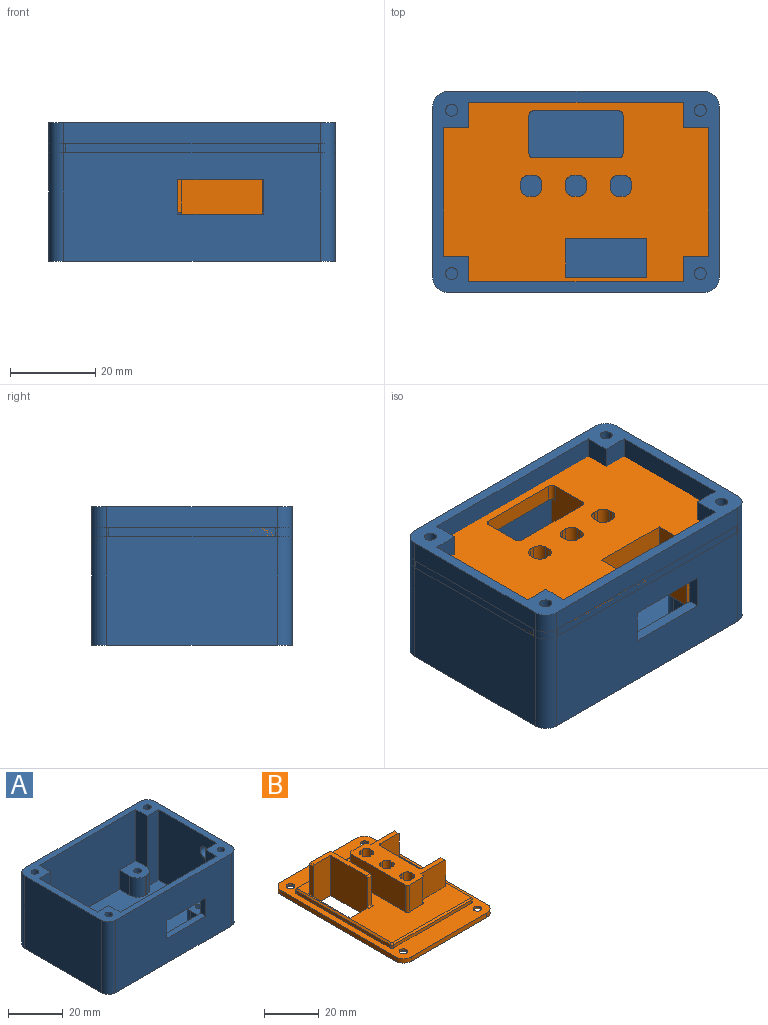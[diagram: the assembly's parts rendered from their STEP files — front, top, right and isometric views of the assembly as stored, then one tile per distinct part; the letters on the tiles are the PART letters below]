
ASSEMBLY  parts=2 mates=1
PART A: 64 faces, bbox 67x47x32.5 mm
  f0: plane 50.15x31.6mm, normal (0,1,0), area 1279mm2, adj f9,f13,f21,f23,f35,f36,f47,f50
  f1: plane 60x32.5mm, normal (0,-1,0), area 1790mm2, adj f13,f14,f17,f18,f59,f60,f61,f62
  f2: plane 50.15x31.6mm, normal (0,-1,0), area 1439mm2, adj f9,f13,f28,f32,f37,f38,f53,f56
  f3: plane 31.6x30.15mm, normal (1,0,0), area 952.7mm2, adj f9,f13,f26,f34
  f4: plane 31.6x30.15mm, normal (-1,0,0), area 933.1mm2, adj f9,f13,f19,f27,f63
  f5: plane 0.53x0.03mm, normal (0,0,1), area 0mm2, adj f27,f41,f53
  f6: plane 0.53x0.03mm, normal (0,0,1), area 0mm2, adj f26,f44,f50
  f7: plane 0.53x0.03mm, normal (0,0,1), area 0mm2, adj f34,f45,f56
  f8: plane 0.53x0.03mm, normal (0,0,1), area 0mm2, adj f19,f39,f47
  f9: plane 62x42mm, normal (0,0,1), area 2172.4mm2, adj f0,f2,f3,f4,f19,f20,f21,f23
  f10: plane 40x32.5mm, normal (1,0,0), area 1280.4mm2, adj f13,f14,f16,f17,f63
  f11: plane 60x32.5mm, normal (0,1,0), area 1950mm2, adj f13,f14,f15,f16
  f12: plane 40x32.5mm, normal (-1,0,0), area 1300mm2, adj f13,f14,f15,f18
  f13: plane 67x47mm, normal (0,0,1), area 650.3mm2, adj f0,f1,f2,f3,f4,f10,f11,f12
  f14: plane 67x47mm, normal (0,0,-1), area 3113.9mm2, adj f1,f10,f11,f12,f15,f16,f17,f18
  f15: cylinder r=3.5mm len=32.5mm, axis (0,0,1), area 178.7mm2, adj f11,f12,f13,f14
  f16: cylinder r=3.5mm len=32.5mm, axis (0,0,-1), area 178.7mm2, adj f10,f11,f13,f14
  f17: cylinder r=3.5mm len=32.5mm, axis (0,0,1), area 178.7mm2, adj f1,f10,f13,f14
  f18: cylinder r=3.5mm len=32.5mm, axis (0,0,-1), area 178.7mm2, adj f1,f12,f13,f14
  f19: plane 31.6x5.96mm, normal (0,1,0), area 187.3mm2, adj f4,f8,f9,f13,f39,f47
  f20: plane 8.6x0.48mm, normal (0,1,0), area 4.1mm2, adj f9,f35,f39,f40
  f21: plane 8.6x5.4mm, normal (-1,0,0), area 46.4mm2, adj f0,f9,f35,f40
  f22: cylinder r=1.4mm len=9.5mm, axis (0,0,1), area 83.6mm2, adj f14,f35
  f23: plane 8.6x5.4mm, normal (1,0,0), area 46.4mm2, adj f0,f9,f36,f43
  f24: plane 8.6x0.48mm, normal (0,1,0), area 4.1mm2, adj f9,f36,f43,f44
  f25: cylinder r=1.4mm len=9.5mm, axis (0,0,1), area 83.6mm2, adj f14,f36
  f26: plane 31.6x5.96mm, normal (0,1,0), area 187.3mm2, adj f3,f6,f9,f13,f44,f50
  f27: plane 31.6x5.96mm, normal (0,-1,0), area 187.3mm2, adj f4,f5,f9,f13,f41,f53
  f28: plane 8.6x5.4mm, normal (-1,0,0), area 46.4mm2, adj f2,f9,f37,f42
  f29: cylinder r=1.4mm len=9.5mm, axis (0,0,1), area 83.6mm2, adj f14,f37
  f30: plane 8.6x0.48mm, normal (0,-1,0), area 4.1mm2, adj f9,f37,f41,f42
  f31: plane 8.6x0.48mm, normal (0,-1,0), area 4.1mm2, adj f9,f38,f45,f46
  f32: plane 8.6x5.4mm, normal (1,0,0), area 46.4mm2, adj f2,f9,f38,f46
  f33: cylinder r=1.4mm len=9.5mm, axis (0,0,1), area 83.6mm2, adj f14,f38
  f34: plane 31.6x5.96mm, normal (0,-1,0), area 187.3mm2, adj f3,f7,f9,f13,f45,f56
  f35: plane 9.4x8.48mm, normal (0,0,1), area 66.6mm2, adj f0,f20,f21,f22,f39,f40,f47
  f36: plane 9.4x8.48mm, normal (0,0,1), area 66.6mm2, adj f0,f23,f24,f25,f43,f44,f50
  f37: plane 9.4x8.48mm, normal (0,0,1), area 66.6mm2, adj f2,f28,f29,f30,f41,f42,f53
  f38: plane 9.4x8.48mm, normal (0,0,1), area 66.6mm2, adj f2,f31,f32,f33,f45,f46,f56
  f39: cylinder r=4mm len=8.6mm, axis (0,0,-1), area 53.2mm2, adj f8,f9,f19,f20,f35,f47
  f40: cylinder r=4mm len=8.6mm, axis (0,0,1), area 54mm2, adj f9,f20,f21,f35
  f41: cylinder r=4mm len=8.6mm, axis (0,0,-1), area 53.2mm2, adj f5,f9,f27,f30,f37,f53
  f42: cylinder r=4mm len=8.6mm, axis (0,0,1), area 54mm2, adj f9,f28,f30,f37
  f43: cylinder r=4mm len=8.6mm, axis (0,0,1), area 54mm2, adj f9,f23,f24,f36
  f44: cylinder r=4mm len=8.6mm, axis (0,0,-1), area 53.2mm2, adj f6,f9,f24,f26,f36,f50
  f45: cylinder r=4mm len=8.6mm, axis (0,0,-1), area 53.2mm2, adj f7,f9,f31,f34,f38,f56
  f46: cylinder r=4mm len=8.6mm, axis (0,0,1), area 54mm2, adj f9,f31,f32,f38
  f47: plane 30x5.93mm, normal (-1,0,0), area 140mm2, adj f0,f8,f13,f19,f35,f39
  f48: plane 2.8x2.8mm, normal (0,0,1), area 6.2mm2, adj f49
  f49: cylinder r=1.4mm len=31.6mm, axis (0,0,1), area 278mm2, adj f13,f48
  f50: plane 30x5.93mm, normal (1,0,0), area 140mm2, adj f0,f6,f13,f26,f36,f44
  f51: plane 2.8x2.8mm, normal (0,0,1), area 6.2mm2, adj f52
  f52: cylinder r=1.4mm len=31.6mm, axis (0,0,1), area 278mm2, adj f13,f51
  f53: plane 30x5.93mm, normal (-1,0,0), area 140mm2, adj f2,f5,f13,f27,f37,f41
  f54: plane 2.8x2.8mm, normal (0,0,1), area 6.2mm2, adj f55
  f55: cylinder r=1.4mm len=31.6mm, axis (0,0,1), area 278mm2, adj f13,f54
  f56: plane 30x5.93mm, normal (1,0,0), area 140mm2, adj f2,f7,f13,f34,f38,f45
  f57: plane 2.8x2.8mm, normal (0,0,1), area 6.2mm2, adj f58
  f58: cylinder r=1.4mm len=31.6mm, axis (0,0,1), area 278mm2, adj f13,f57
  f59: plane 20x2.5mm, normal (0,0,-1), area 50mm2, adj f0,f1,f60,f62
  f60: plane 8x2.5mm, normal (-1,0,0), area 20mm2, adj f0,f1,f59,f61
  f61: plane 20x2.5mm, normal (0,0,1), area 50mm2, adj f0,f1,f60,f62
  f62: plane 8x2.5mm, normal (1,0,0), area 20mm2, adj f0,f1,f59,f61
  f63: cylinder r=2.5mm len=5mm, axis (-1,0,0), area 39.3mm2, adj f4,f10
PART B: 99 faces, bbox 47x67x18 mm
  f0: plane 48.9x40.7mm, normal (0,0,1), area 1132mm2, adj f14,f16,f17,f33,f34,f44,f45,f46
  f1: plane 67x47mm, normal (0,0,-1), area 2559.9mm2, adj f2,f3,f4,f9,f14,f15,f16,f17
  f2: plane 39x2mm, normal (0,1,0), area 78mm2, adj f1,f10,f23,f26
  f3: plane 59x2mm, normal (-1,0,0), area 118mm2, adj f1,f10,f23,f24
  f4: plane 39x2mm, normal (0,-1,0), area 78mm2, adj f1,f10,f24,f25
  f5: cylinder r=1.6mm len=3.2mm, axis (0,0,-1), area 8mm2, adj f10,f28
  f6: cylinder r=1.6mm len=3.2mm, axis (0,0,-1), area 8mm2, adj f10,f30
  f7: cylinder r=1.6mm len=3.2mm, axis (0,0,-1), area 8mm2, adj f10,f27
  f8: cylinder r=1.6mm len=3.2mm, axis (0,0,-1), area 8mm2, adj f10,f29
  f9: plane 59x2mm, normal (1,0,0), area 118mm2, adj f1,f10,f25,f26
  f10: plane 67x47mm, normal (0,0,1), area 1004.8mm2, adj f2,f3,f4,f5,f6,f7,f8,f9
  f11: plane 39.9x1.4mm, normal (0,-1,0), area 55.9mm2, adj f10,f19,f22,f85
  f12: plane 48.1x1.4mm, normal (1,0,0), area 67.3mm2, adj f10,f19,f20,f82
  f13: plane 39.9x1.4mm, normal (0,1,0), area 55.9mm2, adj f10,f20,f21,f86
  f14: plane 16x10mm, normal (0,1,0), area 155.8mm2, adj f0,f1,f31,f34,f51,f56,f97
  f15: plane 20x16mm, normal (1,0,0), area 320mm2, adj f1,f31,f32,f56
  f16: plane 16x10mm, normal (0,-1,0), area 155.8mm2, adj f0,f1,f32,f33,f54,f56,f98
  f17: plane 20x4mm, normal (-1,0,0), area 80mm2, adj f0,f1,f33,f34
  f18: plane 48.1x1.4mm, normal (-1,0,0), area 67.3mm2, adj f10,f21,f22,f89
  f19: cylinder r=1mm len=1.4mm, axis (0,0,1), area 2.2mm2, adj f10,f11,f12,f83
  f20: cylinder r=1mm len=1.4mm, axis (0,0,-1), area 2.2mm2, adj f10,f12,f13,f84
  f21: cylinder r=1mm len=1.4mm, axis (0,0,1), area 2.2mm2, adj f10,f13,f18,f88
  f22: cylinder r=1mm len=1.4mm, axis (0,0,-1), area 2.2mm2, adj f10,f11,f18,f87
  f23: cylinder r=4mm len=4mm, axis (0,0,1), area 12.6mm2, adj f1,f2,f3,f10
  f24: cylinder r=4mm len=4mm, axis (0,0,-1), area 12.6mm2, adj f1,f3,f4,f10
  f25: cylinder r=4mm len=4mm, axis (0,0,1), area 12.6mm2, adj f1,f4,f9,f10
  f26: cylinder r=4mm len=4mm, axis (0,0,-1), area 12.6mm2, adj f1,f2,f9,f10
  f27: cone r=2.8mm half-angle=45deg, axis (0,0,-1), area 23.5mm2, adj f1,f7
  f28: cone r=1.6mm half-angle=45deg, axis (0,0,-1), area 23.5mm2, adj f1,f5
  f29: cone r=1.6mm half-angle=45deg, axis (0,0,-1), area 23.5mm2, adj f1,f8
  f30: cone r=2.8mm half-angle=45deg, axis (0,0,-1), area 23.5mm2, adj f1,f6
  f31: cylinder r=1mm len=16mm, axis (0,0,1), area 25.1mm2, adj f1,f14,f15,f56
  f32: cylinder r=1mm len=16mm, axis (0,0,-1), area 25.1mm2, adj f1,f15,f16,f56
  f33: cylinder r=1mm len=4mm, axis (0,0,-1), area 6.3mm2, adj f0,f1,f16,f17
  f34: cylinder r=1mm len=4mm, axis (0,0,1), area 6.3mm2, adj f0,f1,f14,f17
  f35: plane 16x1mm, normal (0,-1,0), area 16mm2, adj f1,f56,f76,f79
  f36: plane 16x1mm, normal (-1,0,0), area 16mm2, adj f1,f56,f76,f77
  f37: plane 16x1mm, normal (0,1,0), area 16mm2, adj f1,f56,f77,f78
  f38: plane 16x1mm, normal (-1,0,0), area 16mm2, adj f1,f56,f74,f75
  f39: plane 16x1mm, normal (0,1,0), area 16mm2, adj f1,f56,f75,f80
  f40: plane 16x1mm, normal (1,0,0), area 16mm2, adj f1,f56,f80,f81
  f41: plane 16x1mm, normal (0,1,0), area 16mm2, adj f1,f56,f70,f73
  f42: plane 16x1mm, normal (1,0,0), area 16mm2, adj f1,f56,f70,f71
  f43: plane 16x1mm, normal (0,-1,0), area 16mm2, adj f1,f56,f71,f72
  f44: plane 13x12mm, normal (0,1,0), area 155.8mm2, adj f0,f45,f54,f56,f98
  f45: plane 12x1mm, normal (1,0,0), area 12mm2, adj f0,f44,f56,f66
  f46: plane 12x7mm, normal (0,1,0), area 84mm2, adj f0,f56,f66,f67
  f47: plane 28x12mm, normal (-1,0,0), area 336mm2, adj f0,f56,f67,f68
  f48: plane 12x7mm, normal (0,-1,0), area 84mm2, adj f0,f56,f68,f69
  f49: plane 12x1mm, normal (1,0,0), area 12mm2, adj f0,f50,f56,f69
  f50: plane 13x12mm, normal (0,-1,0), area 155.8mm2, adj f0,f49,f51,f56,f97
  f51: plane 11.4x2mm, normal (1,0,0), area 22.8mm2, adj f0,f14,f50,f97
  f52: plane 16x1mm, normal (0,-1,0), area 16mm2, adj f1,f56,f74,f81
  f53: plane 16x1mm, normal (-1,0,0), area 16mm2, adj f1,f56,f72,f73
  f54: plane 11.4x2mm, normal (1,0,0), area 22.8mm2, adj f0,f16,f44,f98
  f55: plane 16x1mm, normal (1,0,0), area 16mm2, adj f1,f56,f78,f79
  f56: plane 30x21.4mm, normal (0,0,1), area 298.5mm2, adj f14,f15,f16,f31,f32,f35,f36,f37
  f57: plane 13.4x10.4mm, normal (0,1,0), area 139.2mm2, adj f58,f63,f90,f91,f96
  f58: plane 13.4x2.6mm, normal (-1,0,0), area 27mm2, adj f0,f57,f59,f91,f96
  f59: plane 18x9mm, normal (0,-1,0), area 161.8mm2, adj f1,f58,f60,f63,f65,f96
  f60: plane 19.6x18mm, normal (-1,0,0), area 342mm2, adj f0,f1,f59,f61,f63,f64,f94,f95
  f61: plane 12.8x2mm, normal (0,-1,0), area 25.6mm2, adj f60,f62,f94,f95
  f62: plane 20.4x13.4mm, normal (1,0,0), area 273.2mm2, adj f61,f63,f90,f93,f95
  f63: plane 20.4x10.4mm, normal (0,0,1), area 57.4mm2, adj f57,f59,f60,f62,f90,f95,f96
  f64: plane 9x4mm, normal (0,1,0), area 36mm2, adj f0,f1,f60,f65
  f65: plane 19x4mm, normal (1,0,0), area 76mm2, adj f0,f1,f59,f64
  f66: cylinder r=1mm len=12mm, axis (0,0,1), area 18.8mm2, adj f0,f45,f46,f56
  f67: cylinder r=1mm len=12mm, axis (0,0,-1), area 18.8mm2, adj f0,f46,f47,f56
  f68: cylinder r=1mm len=12mm, axis (0,0,1), area 18.8mm2, adj f0,f47,f48,f56
  f69: cylinder r=1mm len=12mm, axis (0,0,-1), area 18.8mm2, adj f0,f48,f49,f56
  f70: cylinder r=2mm len=16mm, axis (0,0,1), area 50.3mm2, adj f1,f41,f42,f56
  f71: cylinder r=2mm len=16mm, axis (0,0,1), area 50.3mm2, adj f1,f42,f43,f56
  f72: cylinder r=2mm len=16mm, axis (0,0,-1), area 50.3mm2, adj f1,f43,f53,f56
  f73: cylinder r=2mm len=16mm, axis (0,0,-1), area 50.3mm2, adj f1,f41,f53,f56
  f74: cylinder r=2mm len=16mm, axis (0,0,-1), area 50.3mm2, adj f1,f38,f52,f56
  f75: cylinder r=2mm len=16mm, axis (0,0,1), area 50.3mm2, adj f1,f38,f39,f56
  f76: cylinder r=2mm len=16mm, axis (0,0,1), area 50.3mm2, adj f1,f35,f36,f56
  f77: cylinder r=2mm len=16mm, axis (0,0,1), area 50.3mm2, adj f1,f36,f37,f56
  f78: cylinder r=2mm len=16mm, axis (0,0,-1), area 50.3mm2, adj f1,f37,f55,f56
  f79: cylinder r=2mm len=16mm, axis (0,0,-1), area 50.3mm2, adj f1,f35,f55,f56
  f80: cylinder r=2mm len=16mm, axis (0,0,-1), area 50.3mm2, adj f1,f39,f40,f56
  f81: cylinder r=2mm len=16mm, axis (0,0,1), area 50.3mm2, adj f1,f40,f52,f56
  f82: plane 48.1x0.6mm, normal (0.71,0,0.71), area 40.8mm2, adj f0,f12,f83,f84
  f83: cone r=0.4mm half-angle=45deg, axis (0,0,-1), area 0.9mm2, adj f0,f19,f82,f85
  f84: cone r=0.4mm half-angle=45deg, axis (0,0,-1), area 0.9mm2, adj f0,f20,f82,f86
  f85: plane 39.9x0.6mm, normal (0,-0.71,0.71), area 33.9mm2, adj f0,f11,f83,f87
  f86: plane 39.9x0.6mm, normal (0,0.71,0.71), area 33.9mm2, adj f0,f13,f84,f88
  f87: cone r=0.4mm half-angle=45deg, axis (0,0,-1), area 0.9mm2, adj f0,f22,f85,f89
  f88: cone r=0.4mm half-angle=45deg, axis (0,0,-1), area 0.9mm2, adj f0,f21,f86,f89
  f89: plane 48.1x0.6mm, normal (-0.71,0,0.71), area 40.8mm2, adj f0,f18,f87,f88
  f90: plane 13.4x0.6mm, normal (0.71,0.71,0), area 11.4mm2, adj f57,f62,f63,f92
  f91: plane 10.4x0.6mm, normal (0,0.71,0.71), area 8.8mm2, adj f0,f57,f58,f92
  f92: plane 1.2x1.2mm, normal (0.58,0.58,0.58), area 0.9mm2, adj f0,f90,f91,f93
  f93: plane 21x0.6mm, normal (0.71,0,0.71), area 17.6mm2, adj f0,f62,f92,f94
  f94: plane 2.6x0.6mm, normal (0,-0.71,0.71), area 2mm2, adj f0,f60,f61,f93
  f95: plane 2x0.6mm, normal (0,-0.71,0.71), area 1.7mm2, adj f60,f61,f62,f63
  f96: plane 2x0.6mm, normal (-0.71,0,0.71), area 1.7mm2, adj f57,f58,f59,f63
  f97: plane 2x0.6mm, normal (0.71,0,0.71), area 1.7mm2, adj f14,f50,f51,f56
  f98: plane 2x0.6mm, normal (0.71,0,0.71), area 1.7mm2, adj f16,f44,f54,f56
PLACE A t=(-37.11,11.14,19.72)mm fixed
PLACE B rot(axis=(-0.71,-0.71,0),180deg) t=(-37.11,11.14,44.74)mm
MATE parallel B.f10 <-> A.f13  axis (0,0,-1) through (-3.61,11.14,42.74)mm
